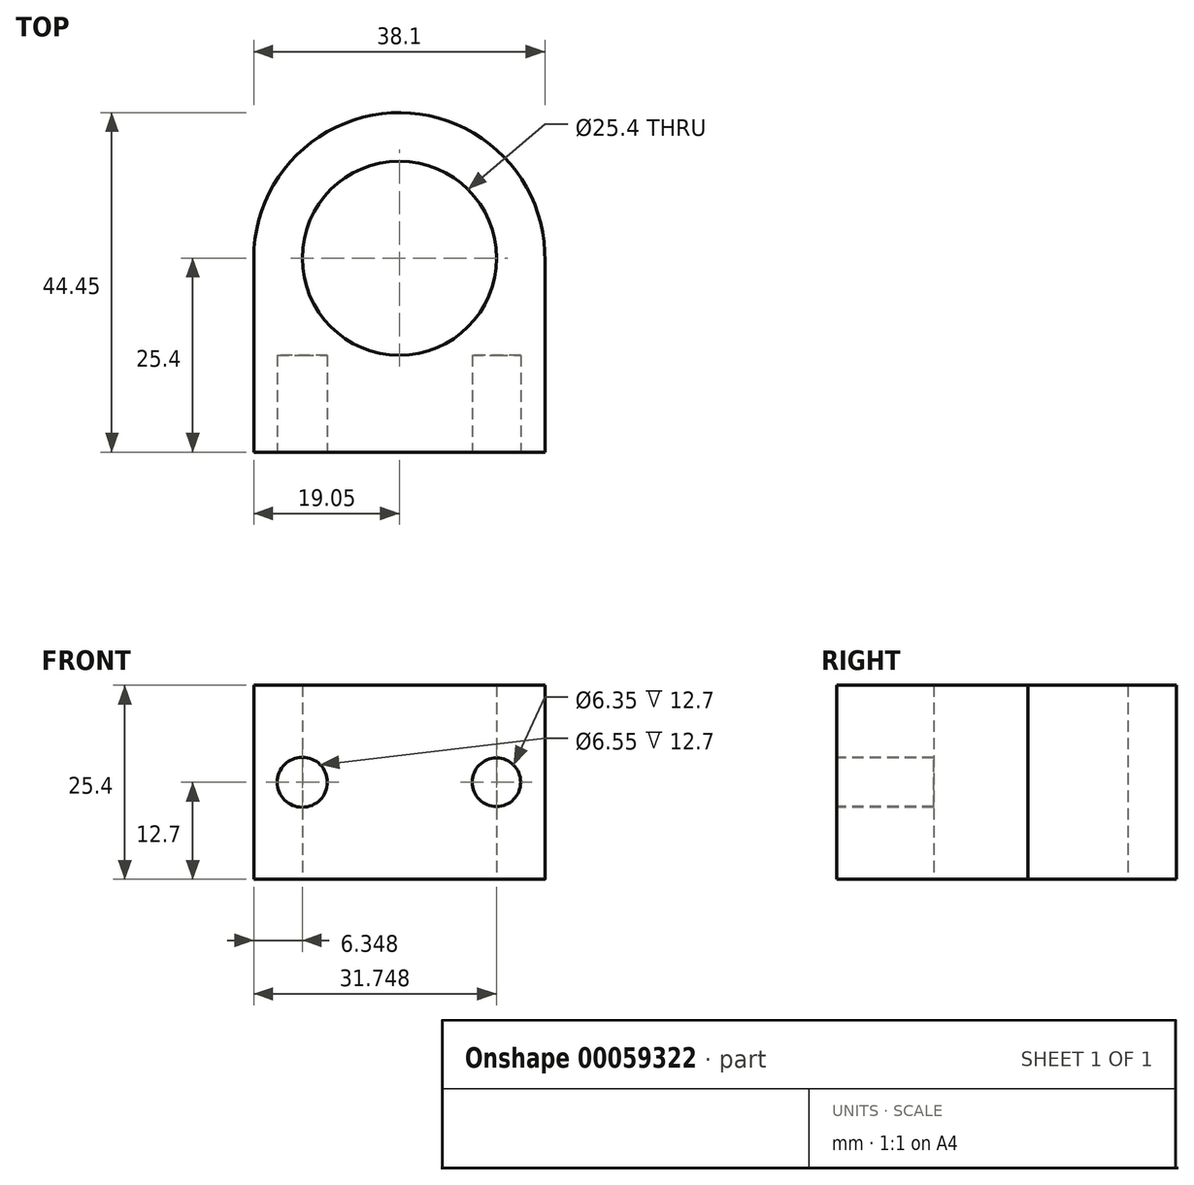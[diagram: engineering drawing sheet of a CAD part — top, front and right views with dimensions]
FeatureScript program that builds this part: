
annotation { "Feature Type Name" : "Feature", "Feature Type Description" : "" }
export const myFeature = defineFeature(function(context is Context, id is Id, definition is map)
    precondition{}
    {
        {
            var Q0;
            Q0=qCreatedBy(makeId("Top.planeOp"),FACE);
            var sketch = newSketch(context, id + "F0", { "sketchPlane" : qUnion([Q0])});
            skArc(sketch, "E0", {"start": v(19.05, -0.37) * mm, "mid": v(0.19, 19.05) * mm, "end": v(-19.05, 0) * mm});
            skCircle(sketch, "E1", {"center": v(0, 0) * mm, "radius": 12.7 * mm});
            skLineSegment(sketch, "E2.top", {"start": v(-19.05, -25.4) * mm, "end": v(19.05, -25.4) * mm});
            skLineSegment(sketch, "E2.left", {"start": v(-19.05, 0) * mm, "end": v(-19.05, -25.4) * mm});
            skLineSegment(sketch, "E2.right", {"start": v(19.05, 0) * mm, "end": v(19.05, -25.4) * mm});
            skSolve(sketch);
        }
        {
            var Q0;
            {var subQ1=sQuery(id+"F0.wireOp",EDGE,"E0");Q0=makeQuery(id+"F0.imprint","IMPRINT",FACE,{"disambiguationData":[TD([[makeQuery(id+"F0.imprint","IMPRINT",EDGE,{"derivedFrom":subQ1}),1.0]])]});}
            extrude(context, id + "F1", {"entities" : qUnion([Q0]), "depth" : 25.4 * mm});
        }
        {
            var Q0;
            Q0=makeQuery(id+"F1.opExtrude","SWEPT_FACE",FACE,{"disambiguationData":[OSD([sQuery(id+"F0.wireOp",EDGE,"E2.top")])]});
            var sketch = newSketch(context, id + "F2", { "sketchPlane" : qUnion([Q0])});
            skCircle(sketch, "E3", {"center": v(-12.7, 12.7) * mm, "radius": 3.28 * mm});
            skCircle(sketch, "E4", {"center": v(12.7, 12.7) * mm, "radius": 3.18 * mm});
            skSolve(sketch);
        }
        {
            var Q0;
            Q0=makeQuery(id+"F2.imprint","IMPRINT",FACE,{"disambiguationData":[TD([[makeQuery(id+"F2.imprint","IMPRINT",EDGE,{"derivedFrom":sQuery(id+"F2.wireOp",EDGE,"E3")}),1.0]])]});
            var Q1;
            Q1=makeQuery(id+"F2.imprint","IMPRINT",FACE,{"disambiguationData":[TD([[makeQuery(id+"F2.imprint","IMPRINT",EDGE,{"derivedFrom":sQuery(id+"F2.wireOp",EDGE,"E4")}),1.0]])]});
            extrude(context, id + "F3", {"entities" : qUnion([Q0, Q1]), "operationType" : NewBodyOperationType.REMOVE, "oppositeDirection" : true, "depth" : 12.7 * mm});
        }
    });
